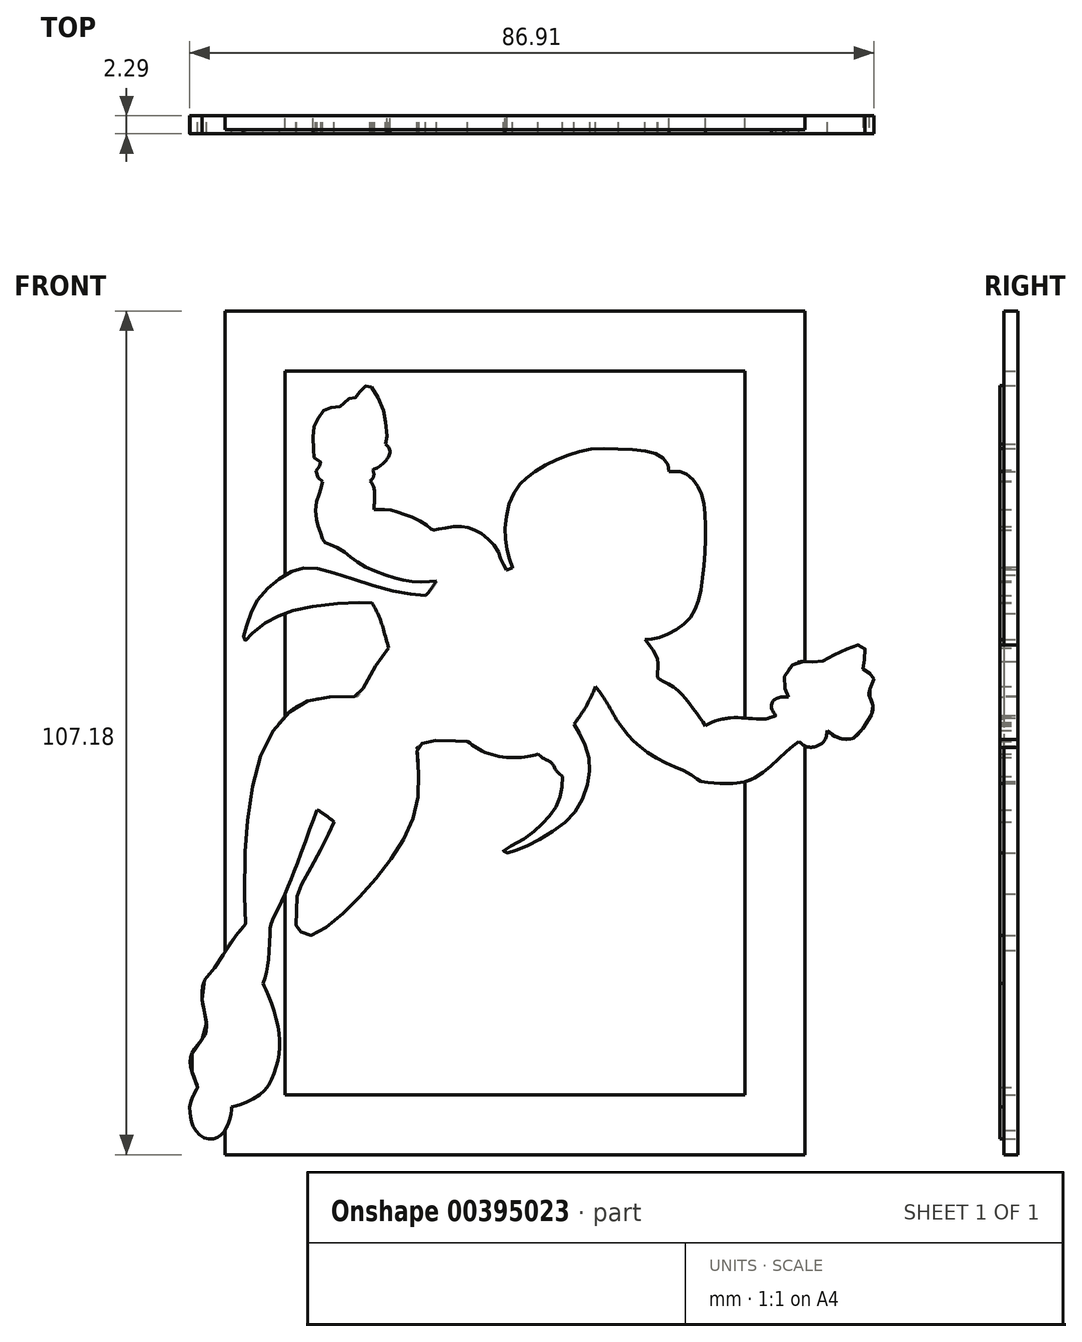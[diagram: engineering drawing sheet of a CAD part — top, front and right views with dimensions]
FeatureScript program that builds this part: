
annotation { "Feature Type Name" : "Feature", "Feature Type Description" : "" }
export const myFeature = defineFeature(function(context is Context, id is Id, definition is map)
    precondition{}
    {
        {
            var Q0;
            Q0=qCreatedBy(makeId("Front.planeOp"),FACE);
            var sketch = newSketch(context, id + "F0", { "sketchPlane" : qUnion([Q0])});
            skLineSegment(sketch, "E0.bottom", {"start": v(36.83, 53.6) * mm, "end": v(-36.83, 53.6) * mm});
            skLineSegment(sketch, "E0.top", {"start": v(36.83, -53.6) * mm, "end": v(-36.83, -53.6) * mm});
            skLineSegment(sketch, "E0.left", {"start": v(36.83, 53.6) * mm, "end": v(36.83, -53.6) * mm});
            skLineSegment(sketch, "E0.right", {"start": v(-36.83, 53.6) * mm, "end": v(-36.83, -53.6) * mm});
            skPoint(sketch, "E0.middle", {"position": v(0, 0) * mm});
            skLineSegment(sketch, "E1.0", {"start": v(-29.2, 45.97) * mm, "end": v(-29.21, -45.97) * mm});
            skLineSegment(sketch, "E1.1", {"start": v(29.21, 45.97) * mm, "end": v(-29.21, 45.97) * mm});
            skLineSegment(sketch, "E1.2", {"start": v(29.21, 45.97) * mm, "end": v(29.21, -45.97) * mm});
            skLineSegment(sketch, "E1.3", {"start": v(29.21, -45.97) * mm, "end": v(-29.21, -45.97) * mm});
            skSolve(sketch);
        }
        {
            var Q0;
            Q0 = qSketchRegion(id + "F0", true);
            extrude(context, id + "F1", {"entities" : qUnion([Q0]), "depth" : 1.78 * mm});
        }
        {
            var Q0;
            Q0=qCreatedBy(makeId("Front.planeOp"),FACE);
            var sketch = newSketch(context, id + "F2", { "sketchPlane" : qUnion([Q0])});
            skFitSpline(sketch, "E2", {"points": [v(-40.3, -45.01) * mm, v(-40.78, -45.94) * mm, v(-41.27, -47.24) * mm, v(-41.23, -48.72) * mm, v(-40.76, -50.17) * mm, v(-39.5, -51.43) * mm, v(-38.13, -51.53) * mm, v(-37.16, -50.92) * mm, v(-36.37, -49.6) * mm, v(-36.03, -48.23) * mm, v(-36, -47.52) * mm], "startDerivative": vector(-5.33, -9.98) * mm, "endDerivative": vector(0.13, 8.86) * mm});
            skFitSpline(sketch, "E3", {"points": [v(-36, -47.52) * mm, v(-34.5, -47.1) * mm, v(-32, -45.62) * mm, v(-30.71, -43.56) * mm, v(-29.96, -40.93) * mm, v(-29.96, -38.24) * mm, v(-30.8, -34.72) * mm, v(-31.82, -32.2) * mm, v(-32.03, -31.86) * mm], "startDerivative": vector(13.23, 2.92) * mm, "endDerivative": vector(-3.23, 4.91) * mm});
            skFitSpline(sketch, "E4", {"points": [v(-32.03, -31.86) * mm, v(-31.5, -30.26) * mm, v(-31.28, -28.32) * mm, v(-31.1, -25.2) * mm, v(-30.92, -24.15) * mm, v(-29.63, -21.38) * mm, v(-28.47, -18.67) * mm, v(-27.04, -14.93) * mm, v(-25.25, -10.08) * mm, v(-25.1, -9.78) * mm], "startDerivative": vector(6.34, 17.06) * mm, "endDerivative": vector(2.36, 4.7) * mm});
            skFitSpline(sketch, "E5", {"points": [v(-25.1, -9.78) * mm, v(-24.1, -10.44) * mm, v(-22.95, -11.3) * mm], "startDerivative": vector(2.08, -1.33) * mm, "endDerivative": vector(2.24, -1.73) * mm});
            skFitSpline(sketch, "E6", {"points": [v(-22.95, -11.3) * mm, v(-23.51, -12.48) * mm, v(-24.6, -14.63) * mm, v(-26.08, -17.48) * mm, v(-27.37, -19.78) * mm, v(-27.68, -20.85) * mm, v(-27.73, -22.57) * mm, v(-27.76, -24.4) * mm, v(-27.76, -24.65) * mm, v(-27.32, -25.16) * mm, v(-26.57, -25.63) * mm, v(-25.47, -25.65) * mm, v(-22.95, -23.9) * mm, v(-19.92, -21.07) * mm, v(-16.69, -17.3) * mm, v(-14.19, -13.64) * mm, v(-12.6, -9.78) * mm, v(-12.22, -5.78) * mm, v(-12.42, -2.04) * mm, v(-12.35, -1.78) * mm, v(-11.33, -1.14) * mm, v(-9.56, -0.98) * mm, v(-6.62, -1.07) * mm, v(-6, -1.1) * mm], "startDerivative": vector(-14.69, -31.4) * mm, "endDerivative": vector(19.63, -1.39) * mm});
            skFitSpline(sketch, "E7", {"points": [v(-6, -1.1) * mm, v(-4.46, -2.16) * mm, v(-1.77, -3.04) * mm, v(1.26, -3.08) * mm, v(2.92, -2.72) * mm], "startDerivative": vector(6.31, -4.9) * mm, "endDerivative": vector(7.12, 1.91) * mm});
            skFitSpline(sketch, "E8", {"points": [v(2.92, -2.72) * mm, v(3.83, -3.35) * mm, v(4.71, -3.86) * mm, v(5.19, -4.7) * mm, v(6.07, -5.54) * mm], "startDerivative": vector(3.4, -2.71) * mm, "endDerivative": vector(3.82, -2.9) * mm});
            skFitSpline(sketch, "E9", {"points": [v(6.07, -5.54) * mm, v(5.9, -7.28) * mm, v(5.4, -9.01) * mm, v(4.28, -10.68) * mm, v(2.92, -12.07) * mm, v(1.1, -13.49) * mm, v(-1.35, -14.88) * mm, v(-1.46, -15.07) * mm, v(-1.12, -15.24) * mm, v(-0.19, -15.03) * mm, v(2.1, -14.12) * mm, v(5.32, -12.14) * mm, v(7.87, -9.78) * mm, v(9.27, -6.32) * mm, v(9.44, -3.47) * mm, v(8.52, -0.66) * mm, v(7.48, 1.1) * mm], "startDerivative": vector(-2.1, -30.1) * mm, "endDerivative": vector(-16.87, 26.04) * mm});
            skFitSpline(sketch, "E10", {"points": [v(7.48, 1.1) * mm, v(8.42, 2.38) * mm, v(9.75, 4.68) * mm, v(10.2, 5.87) * mm], "startDerivative": vector(2.8, 3.6) * mm, "endDerivative": vector(1.25, 3.81) * mm});
            skFitSpline(sketch, "E11", {"points": [v(10.2, 5.87) * mm, v(11.28, 4.46) * mm, v(12.76, 1.93) * mm, v(13.13, 1.33) * mm], "startDerivative": vector(2.94, -3.48) * mm, "endDerivative": vector(1.43, -2.13) * mm});
            skFitSpline(sketch, "E12", {"points": [v(13.13, 1.33) * mm, v(13.98, 0.22) * mm, v(14.91, -0.89) * mm, v(16.07, -1.92) * mm, v(18, -3.2) * mm, v(20.09, -4.23) * mm, v(21.82, -4.98) * mm, v(23.02, -5.77) * mm, v(23.43, -6.06) * mm, v(23.98, -6.25) * mm, v(26.75, -6.44) * mm, v(29.78, -6.04) * mm, v(31.75, -4.86) * mm, v(33.51, -3.3) * mm, v(35.12, -1.83) * mm, v(36.06, -1.1) * mm], "startDerivative": vector(13.91, -18.54) * mm, "endDerivative": vector(16.03, 11.7) * mm});
            skFitSpline(sketch, "E13", {"points": [v(36.06, -1.1) * mm, v(36.47, -1.42) * mm, v(37.02, -1.76) * mm, v(38.35, -1.7) * mm, v(39.32, -0.99) * mm, v(39.58, -0.32) * mm, v(39.7, 0.3) * mm], "startDerivative": vector(3.06, -2.29) * mm, "endDerivative": vector(0.77, 4.22) * mm});
            skFitSpline(sketch, "E14", {"points": [v(39.7, 0.3) * mm, v(40.44, -0.31) * mm, v(40.99, -0.58) * mm, v(41.55, -0.78) * mm, v(42.73, -0.78) * mm, v(44, 0.3) * mm, v(45.31, 2.4) * mm, v(45.5, 3.27) * mm, v(45.27, 4.22) * mm, v(45.01, 4.62) * mm, v(45, 5.33) * mm, v(45.48, 6.53) * mm, v(45.58, 7.01) * mm, v(45.31, 7.4) * mm, v(44.55, 7.82) * mm, v(44.18, 8.2) * mm, v(44.38, 9.11) * mm, v(44.49, 10.33) * mm, v(44.32, 10.96) * mm, v(43.5, 11.16) * mm, v(42.12, 10.65) * mm, v(40.32, 9.78) * mm, v(39.04, 9.1) * mm, v(37.85, 8.97) * mm, v(37.06, 9.01) * mm, v(36.06, 9) * mm, v(34.67, 8.04) * mm, v(34.15, 6.38) * mm, v(34.43, 5.17) * mm, v(34.74, 4.56) * mm], "startDerivative": vector(22.5, -20.66) * mm, "endDerivative": vector(10.79, -19.67) * mm});
            skFitSpline(sketch, "E15", {"points": [v(34.74, 4.56) * mm, v(33.99, 4.56) * mm, v(33.1, 4.28) * mm, v(32.67, 3.8) * mm, v(32.66, 2.97) * mm, v(33.06, 2.3) * mm, v(33.18, 2.2) * mm], "startDerivative": vector(-4, 0.28) * mm, "endDerivative": vector(1.25, -0.88) * mm});
            skFitSpline(sketch, "E16", {"points": [v(33.18, 2.2) * mm, v(32.44, 1.94) * mm, v(31.69, 1.76) * mm, v(29.52, 1.85) * mm, v(27.36, 1.89) * mm, v(25, 1.33) * mm, v(24.22, 0.9) * mm], "startDerivative": vector(-6.23, -2.23) * mm, "endDerivative": vector(-4.82, -3.32) * mm});
            skFitSpline(sketch, "E17", {"points": [v(24.22, 0.9) * mm, v(23.3, 2.2) * mm, v(21.83, 4.13) * mm, v(20.38, 5.67) * mm, v(18.7, 6.64) * mm, v(18.21, 6.95) * mm, v(18.1, 7.17) * mm, v(18.15, 8.18) * mm, v(18.07, 9.5) * mm, v(17.18, 11) * mm, v(16.53, 11.86) * mm], "startDerivative": vector(-7.83, 11.11) * mm, "endDerivative": vector(-6.54, 8.74) * mm});
            skFitSpline(sketch, "E18", {"points": [v(16.53, 11.86) * mm, v(18, 12.02) * mm, v(20.3, 12.97) * mm, v(22.24, 14.61) * mm, v(23.33, 16.92) * mm, v(23.96, 20.98) * mm, v(24.22, 26.04) * mm, v(23.88, 29.74) * mm, v(22.97, 31.7) * mm, v(21.47, 33.04) * mm, v(20.24, 33.18) * mm, v(19.57, 33.18) * mm], "startDerivative": vector(19.3, 0.77) * mm, "endDerivative": vector(-12.81, 0.2) * mm});
            skFitSpline(sketch, "E19", {"points": [v(19.57, 33.18) * mm, v(19.39, 34.17) * mm, v(18.54, 35.08) * mm, v(16.98, 35.73) * mm, v(13.46, 36.04) * mm, v(9.92, 36.06) * mm, v(7.27, 35.45) * mm, v(4.64, 34.4) * mm, v(2.1, 32.86) * mm, v(0.78, 31.75) * mm, v(-0.42, 29.93) * mm, v(-1.17, 26.95) * mm, v(-1.2, 24.6) * mm, v(-0.82, 22.56) * mm, v(-0.28, 20.98) * mm], "startDerivative": vector(-1.11, 21.37) * mm, "endDerivative": vector(9.43, -24.71) * mm});
            skFitSpline(sketch, "E20", {"points": [v(-0.28, 20.98) * mm, v(-0.66, 20.82) * mm, v(-1.06, 20.68) * mm], "startDerivative": vector(-0.77, -0.34) * mm, "endDerivative": vector(-0.81, -0.27) * mm});
            skFitSpline(sketch, "E21", {"points": [v(-1.06, 20.68) * mm, v(-1.7, 21.83) * mm, v(-2.28, 23.31) * mm, v(-3.88, 25.01) * mm, v(-5.58, 25.96) * mm, v(-7, 26.22) * mm, v(-9.04, 26) * mm, v(-10.23, 25.78) * mm, v(-10.43, 25.74) * mm, v(-10.9, 26.12) * mm, v(-12.53, 27.17) * mm, v(-14.58, 27.9) * mm, v(-15.93, 28.35) * mm, v(-17.33, 28.37) * mm, v(-17.92, 28.37) * mm], "startDerivative": vector(-9.8, 15.76) * mm, "endDerivative": vector(-10.94, 0.26) * mm});
            skFitSpline(sketch, "E22", {"points": [v(-17.92, 28.37) * mm, v(-17.83, 29.6) * mm, v(-17.92, 31.16) * mm, v(-18.37, 31.99) * mm], "startDerivative": vector(0.3, 3.5) * mm, "endDerivative": vector(-1.85, 2.5) * mm});
            skFitSpline(sketch, "E23", {"points": [v(-18.37, 31.99) * mm, v(-18.06, 32.35) * mm, v(-17.92, 32.88) * mm, v(-18.06, 33.4) * mm], "startDerivative": vector(1.07, 1.03) * mm, "endDerivative": vector(-0.6, 1.52) * mm});
            skFitSpline(sketch, "E24", {"points": [v(-18.06, 33.4) * mm, v(-17.17, 33.85) * mm, v(-16.4, 34.6) * mm, v(-15.96, 35.26) * mm, v(-15.98, 36.15) * mm, v(-16.44, 36.66) * mm], "startDerivative": vector(4.32, 1.74) * mm, "endDerivative": vector(-3.13, 2.4) * mm});
            skFitSpline(sketch, "E25", {"points": [v(-16.44, 36.66) * mm, v(-16.26, 37.39) * mm, v(-16.44, 39.65) * mm, v(-16.89, 41.47) * mm, v(-18.06, 43.7) * mm, v(-18.59, 44.1) * mm, v(-19.05, 44) * mm, v(-19.7, 43.3) * mm, v(-20.06, 42.75) * mm, v(-20.5, 42.49) * mm, v(-21.15, 42.42) * mm, v(-21.56, 42.08) * mm, v(-21.82, 41.68) * mm, v(-22.15, 41.45) * mm, v(-23.04, 41.33) * mm, v(-23.99, 41.21) * mm, v(-24.7, 40.46) * mm, v(-25.3, 39.4) * mm, v(-25.6, 38.44) * mm, v(-25.63, 36.52) * mm, v(-25.54, 35.14) * mm, v(-25.44, 34.92) * mm, v(-24.67, 34.37) * mm, v(-24.61, 34.23) * mm, v(-24.7, 33.99) * mm, v(-25.14, 33.7) * mm, v(-25.28, 33.08) * mm, v(-25.1, 32.57) * mm, v(-24.65, 32.1) * mm, v(-24.45, 31.95) * mm], "startDerivative": vector(7.06, 17.85) * mm, "endDerivative": vector(9.22, -6.22) * mm});
            skFitSpline(sketch, "E26", {"points": [v(-24.45, 31.95) * mm, v(-24.72, 30.77) * mm, v(-25.22, 29.36) * mm, v(-25.22, 27.2) * mm, v(-24.88, 25.94) * mm, v(-24.45, 24.72) * mm, v(-24.2, 24.26) * mm, v(-23.56, 23.94) * mm, v(-21.98, 23.19) * mm, v(-20.6, 22.11) * mm, v(-18.6, 20.9) * mm, v(-15.67, 19.83) * mm, v(-13.71, 19.3) * mm, v(-11.44, 19.18) * mm, v(-9.95, 19.3) * mm], "startDerivative": vector(-3.11, -19.08) * mm, "endDerivative": vector(20.2, 2.25) * mm});
            skFitSpline(sketch, "E27", {"points": [v(-9.95, 19.3) * mm, v(-10.76, 18.1) * mm, v(-11.34, 17.44) * mm], "startDerivative": vector(-1.48, -2.3) * mm, "endDerivative": vector(-1.3, -1.38) * mm});
            skFitSpline(sketch, "E28", {"points": [v(-11.34, 17.44) * mm, v(-13.9, 17.7) * mm, v(-17.99, 18.7) * mm, v(-22.43, 20.13) * mm, v(-25.44, 20.9) * mm, v(-27.35, 20.86) * mm, v(-29.1, 20.1) * mm, v(-31.03, 18.68) * mm, v(-32.67, 16.9) * mm, v(-33.54, 15.18) * mm, v(-34.26, 12.97) * mm, v(-34.53, 12.06) * mm, v(-34.49, 11.8) * mm, v(-34.22, 11.76) * mm, v(-33.74, 12.28) * mm, v(-31.57, 14.04) * mm, v(-29.49, 15.07) * mm, v(-26.2, 15.99) * mm, v(-20.08, 16.53) * mm, v(-18.15, 16.5) * mm], "startDerivative": vector(-42.33, 2.89) * mm, "endDerivative": vector(32.1, -1.6) * mm});
            skFitSpline(sketch, "E29", {"points": [v(-18.15, 16.5) * mm, v(-17.34, 14.95) * mm, v(-16.75, 13.29) * mm, v(-16.05, 10.76) * mm], "startDerivative": vector(2.82, -5) * mm, "endDerivative": vector(1.9, -7.03) * mm});
            skFitSpline(sketch, "E30", {"points": [v(-16.05, 10.76) * mm, v(-17.53, 8.78) * mm, v(-19.2, 5.9) * mm, v(-19.96, 4.6) * mm, v(-20.1, 4.58) * mm, v(-22.48, 4.6) * mm, v(-25.46, 4.29) * mm, v(-27.37, 3.52) * mm, v(-29.5, 1.89) * mm, v(-31.52, -1.17) * mm, v(-33.01, -5.27) * mm, v(-33.95, -11.1) * mm, v(-34.33, -16.85) * mm, v(-34.24, -24.15) * mm, v(-34.27, -24.38) * mm, v(-35.04, -25.35) * mm, v(-36.47, -26.98) * mm, v(-37.7, -29.53) * mm, v(-37.99, -29.73) * mm, v(-38.96, -30.73) * mm, v(-39.48, -31.56) * mm, v(-39.73, -33.64) * mm, v(-39.25, -36.5) * mm, v(-39.3, -38.25) * mm, v(-40.08, -39.34) * mm, v(-41.02, -40.74) * mm, v(-41.22, -42.43) * mm, v(-40.53, -44.32) * mm, v(-40.3, -45.01) * mm], "startDerivative": vector(-38.64, -47.42) * mm, "endDerivative": vector(8.26, -28.9) * mm});
            skSolve(sketch);
        }
        {
            var Q0;
            Q0 = qSketchRegion(id + "F2", true);
            extrude(context, id + "F3", {"entities" : qUnion([Q0]), "operationType" : NewBodyOperationType.ADD, "depth" : 2.3 * mm});
        }
        {
            var Q0;
            Q0=makeQuery(id+"F3.opExtrude","CAP_FACE",FACE,{"disambiguationData":[OSD([sQuery(id+"F2.wireOp",EDGE,"E2"),sQuery(id+"F2.wireOp",EDGE,"E3"),sQuery(id+"F2.wireOp",EDGE,"E4"),sQuery(id+"F2.wireOp",EDGE,"E5"),sQuery(id+"F2.wireOp",EDGE,"E6"),sQuery(id+"F2.wireOp",EDGE,"E7"),sQuery(id+"F2.wireOp",EDGE,"E8"),sQuery(id+"F2.wireOp",EDGE,"E9"),sQuery(id+"F2.wireOp",EDGE,"E10"),sQuery(id+"F2.wireOp",EDGE,"E11"),sQuery(id+"F2.wireOp",EDGE,"E12"),sQuery(id+"F2.wireOp",EDGE,"E13"),sQuery(id+"F2.wireOp",EDGE,"E14"),sQuery(id+"F2.wireOp",EDGE,"E15"),sQuery(id+"F2.wireOp",EDGE,"E16"),sQuery(id+"F2.wireOp",EDGE,"E17"),sQuery(id+"F2.wireOp",EDGE,"E18"),sQuery(id+"F2.wireOp",EDGE,"E19"),sQuery(id+"F2.wireOp",EDGE,"E20"),sQuery(id+"F2.wireOp",EDGE,"E21"),sQuery(id+"F2.wireOp",EDGE,"E22"),sQuery(id+"F2.wireOp",EDGE,"E23"),sQuery(id+"F2.wireOp",EDGE,"E24"),sQuery(id+"F2.wireOp",EDGE,"E25"),sQuery(id+"F2.wireOp",EDGE,"E26"),sQuery(id+"F2.wireOp",EDGE,"E27"),sQuery(id+"F2.wireOp",EDGE,"E28"),sQuery(id+"F2.wireOp",EDGE,"E29"),sQuery(id+"F2.wireOp",EDGE,"E30")])],"isStart":false});
            var sketch = newSketch(context, id + "F4", { "sketchPlane" : qUnion([Q0])});
            skFitSpline(sketch, "E31", {"points": [v(6.33, 20.8) * mm, v(6.52, 21.07) * mm, v(6.8, 21.26) * mm, v(7.13, 21.28) * mm], "startDerivative": vector(0.5, 0.86) * mm, "endDerivative": vector(1.04, -0.07) * mm});
            skFitSpline(sketch, "E32", {"points": [v(14.02, 16.77) * mm, v(13.22, 16.62) * mm, v(12.18, 16.57) * mm, v(10.86, 16.87) * mm, v(9.92, 17.2) * mm], "startDerivative": vector(-3.53, -0.74) * mm, "endDerivative": vector(-3.62, 1.3) * mm});
            skFitSpline(sketch, "E33", {"points": [v(7.1, 20.4) * mm, v(7.64, 19.66) * mm, v(8.02, 19.03) * mm, v(8.36, 18.6) * mm], "startDerivative": vector(1.56, -1.95) * mm, "endDerivative": vector(1.2, -1.43) * mm});
            skFitSpline(sketch, "E34", {"points": [v(6.9, 19.34) * mm, v(6.9, 18.4) * mm, v(7.15, 17.57) * mm, v(7.93, 16.58) * mm, v(8.88, 15.8) * mm, v(10.1, 15.46) * mm, v(11.16, 15.78) * mm, v(11.72, 16.41) * mm], "startDerivative": vector(-0.34, -7.15) * mm, "endDerivative": vector(3.77, 5.4) * mm});
            skFitSpline(sketch, "E35", {"points": [v(7.91, 20.38) * mm, v(9.12, 19.93) * mm, v(10.45, 19.19) * mm, v(11.45, 18.49) * mm, v(12.05, 17.8) * mm, v(12.63, 17.06) * mm, v(13.1, 16.79) * mm], "startDerivative": vector(6.48, -2.05) * mm, "endDerivative": vector(4, -1.7) * mm});
            skFitSpline(sketch, "E36", {"points": [v(13.88, 17.14) * mm, v(14.14, 16.89) * mm, v(14.26, 16.6) * mm], "startDerivative": vector(0.56, -0.46) * mm, "endDerivative": vector(0.19, -0.63) * mm});
            skCircle(sketch, "E37", {"center": v(11.13, 20.67) * mm, "radius": 0.18 * mm});
            skCircle(sketch, "E38", {"center": v(11.88, 19.95) * mm, "radius": 0.28 * mm});
            skFitSpline(sketch, "E39", {"points": [v(10.55, 26.04) * mm, v(10.32, 25.81) * mm, v(10.08, 25.47) * mm, v(10.16, 25) * mm, v(10.4, 24.68) * mm, v(11.07, 24.88) * mm, v(11.21, 25.05) * mm], "startDerivative": vector(-1.43, -1.43) * mm, "endDerivative": vector(0.7, 1.26) * mm});
            skFitSpline(sketch, "E40", {"points": [v(8.8, 25.47) * mm, v(8.93, 26.06) * mm, v(9.45, 26.44) * mm, v(10.32, 26.48) * mm, v(11, 25.83) * mm, v(11.4, 25.2) * mm, v(11.58, 24.26) * mm], "startDerivative": vector(0.26, 4.34) * mm, "endDerivative": vector(0.61, -5.55) * mm});
            skFitSpline(sketch, "E41", {"points": [v(15.32, 22.5) * mm, v(15.12, 22.03) * mm, v(15.08, 21.5) * mm, v(15.4, 21.28) * mm, v(15.95, 21.28) * mm, v(16.45, 21.85) * mm, v(16.57, 22.05) * mm], "startDerivative": vector(-1.27, -2.54) * mm, "endDerivative": vector(0.81, 1.4) * mm});
            skFitSpline(sketch, "E42", {"points": [v(14.17, 22.11) * mm, v(14.96, 22.52) * mm, v(15.54, 22.68) * mm, v(16.41, 22.5) * mm, v(17.12, 21.87) * mm, v(17.3, 21.28) * mm, v(17.1, 20.84) * mm, v(16.57, 20.53) * mm], "startDerivative": vector(5.17, 2.8) * mm, "endDerivative": vector(-4.44, -1.94) * mm});
            skFitSpline(sketch, "E43", {"points": [v(9.88, 28.02) * mm, v(10.79, 28.38) * mm, v(12.08, 28.65) * mm, v(12.59, 28.63) * mm, v(12.83, 28.44) * mm, v(12.77, 27.88) * mm, v(12.71, 26.7) * mm, v(12.81, 26.06) * mm, v(13.2, 25.81) * mm, v(13.62, 25.77) * mm], "startDerivative": vector(6.17, 2.86) * mm, "endDerivative": vector(4.76, -0.05) * mm});
            skFitSpline(sketch, "E44", {"points": [v(15.62, 24.34) * mm, v(15.93, 24.07) * mm, v(16.55, 24.18) * mm, v(17.44, 24.64) * mm, v(18.1, 25.05) * mm, v(18.3, 25.07) * mm, v(18.46, 24.92) * mm, v(18.5, 24.66) * mm], "startDerivative": vector(1.95, -2.5) * mm, "endDerivative": vector(0.03, -2.59) * mm});
            skFitSpline(sketch, "E45", {"points": [v(17.32, 28.18) * mm, v(18.31, 28.63) * mm, v(19.47, 28.93) * mm, v(20.28, 28.93) * mm], "startDerivative": vector(2.77, 1.35) * mm, "endDerivative": vector(2.6, -0.18) * mm});
            skFitSpline(sketch, "E46", {"points": [v(10.75, 33.85) * mm, v(10.24, 33.28) * mm, v(10.02, 32.71) * mm, v(10.04, 32.6) * mm, v(10.85, 32.87) * mm, v(12.23, 33.14) * mm, v(12.55, 33.22) * mm, v(12.71, 33.3) * mm, v(13.03, 33.8) * mm, v(13.28, 34.19) * mm, v(13.26, 34.31) * mm, v(12.75, 34.2) * mm, v(12.02, 34.17) * mm, v(11.17, 34.09) * mm, v(10.75, 33.85) * mm]});
            skFitSpline(sketch, "E47", {"points": [v(-0.1, 20.83) * mm, v(0.34, 20.08) * mm, v(1.4, 19.03) * mm, v(2.69, 18.14) * mm, v(4.57, 17.92) * mm, v(5.74, 18.08) * mm, v(5.83, 18.16) * mm, v(5.66, 18.26) * mm, v(4.87, 18.93) * mm, v(4.02, 20.49) * mm, v(4.07, 22.2) * mm, v(5.48, 25.12) * mm, v(7.12, 26.98) * mm, v(9.59, 29.03) * mm, v(13.2, 30.48) * mm, v(15.03, 30.8) * mm, v(15.93, 30.6) * mm, v(15.93, 29.96) * mm, v(15.7, 29.09) * mm, v(15.68, 28.68) * mm], "startDerivative": vector(8.68, -17.41) * mm, "endDerivative": vector(0.36, -12.73) * mm});
            skFitSpline(sketch, "E48", {"points": [v(17.74, 27.25) * mm, v(18.67, 27.49) * mm, v(19.97, 27.37) * mm, v(20.15, 26.86) * mm, v(19.82, 24.45) * mm, v(19.01, 22.15) * mm, v(18.1, 19.68) * mm, v(17.17, 17.88) * mm, v(15.93, 16.32) * mm, v(14.73, 15.35) * mm, v(13.2, 14.44) * mm, v(12.64, 14.26) * mm, v(12.14, 14.18) * mm, v(9.83, 14.08) * mm, v(9.04, 13.87) * mm, v(8.15, 14.04) * mm, v(7, 14.72) * mm, v(5.93, 15.65) * mm, v(5.7, 16.32) * mm, v(5.36, 17.03) * mm, v(5.16, 17.62) * mm], "startDerivative": vector(19, 6.88) * mm, "endDerivative": vector(-4.68, 16.61) * mm});
            skFitSpline(sketch, "E49", {"points": [v(16.37, 11.86) * mm, v(15.2, 12.01) * mm, v(13.89, 12.36) * mm, v(12.64, 12.97) * mm, v(11.88, 13.56) * mm], "startDerivative": vector(-4.7, 0.48) * mm, "endDerivative": vector(-3.15, 2.68) * mm});
            skSolve(sketch);
        }
        {
            var Q0;
            Q0 = qSketchRegion(id + "F4", true);
            var Q1;
            Q1=sQuery(id+"F4.wireOp",EDGE,"E47");
            var Q2;
            Q2=sQuery(id+"F4.wireOp",EDGE,"E48");
            var Q3;
            Q3=sQuery(id+"F4.wireOp",EDGE,"E34");
            var Q4;
            Q4=sQuery(id+"F4.wireOp",EDGE,"E32");
            var Q5;
            Q5=sQuery(id+"F4.wireOp",EDGE,"E46");
            var Q6;
            Q6=sQuery(id+"F4.wireOp",EDGE,"E38");
            var Q7;
            Q7=sQuery(id+"F4.wireOp",EDGE,"E37");
            var Q8;
            Q8=sQuery(id+"F4.wireOp",EDGE,"E35");
            var Q9;
            Q9=sQuery(id+"F4.wireOp",EDGE,"E33");
            var Q10;
            Q10=sQuery(id+"F4.wireOp",EDGE,"E31");
            var Q11;
            Q11=sQuery(id+"F4.wireOp",EDGE,"E36");
            var Q12;
            Q12=sQuery(id+"F4.wireOp",EDGE,"E41");
            var Q13;
            Q13=sQuery(id+"F4.wireOp",EDGE,"E42");
            var Q14;
            Q14=sQuery(id+"F4.wireOp",EDGE,"E44");
            var Q15;
            Q15=sQuery(id+"F4.wireOp",EDGE,"E45");
            var Q16;
            Q16=sQuery(id+"F4.wireOp",EDGE,"E43");
            var Q17;
            Q17=sQuery(id+"F4.wireOp",EDGE,"E39");
            var Q18;
            Q18=sQuery(id+"F4.wireOp",EDGE,"E40");
            var Q19;
            Q19=sQuery(id+"F4.wireOp",EDGE,"E49");
            extrude(context, id + "F5", {"entities" : qUnion([Q0]), "bodyType" : ToolBodyType.SURFACE, "surfaceEntities" : qUnion([Q1, Q2, Q3, Q4, Q5, Q6, Q7, Q8, Q9, Q10, Q11, Q12, Q13, Q14, Q15, Q16, Q17, Q18, Q19]), "depth" : 0.25 * mm});
        }
        {
            var Q0;
            Q0=makeQuery(id+"F3.opExtrude","CAP_FACE",FACE,{"disambiguationData":[OSD([sQuery(id+"F2.wireOp",EDGE,"E2"),sQuery(id+"F2.wireOp",EDGE,"E3"),sQuery(id+"F2.wireOp",EDGE,"E4"),sQuery(id+"F2.wireOp",EDGE,"E5"),sQuery(id+"F2.wireOp",EDGE,"E6"),sQuery(id+"F2.wireOp",EDGE,"E7"),sQuery(id+"F2.wireOp",EDGE,"E8"),sQuery(id+"F2.wireOp",EDGE,"E9"),sQuery(id+"F2.wireOp",EDGE,"E10"),sQuery(id+"F2.wireOp",EDGE,"E11"),sQuery(id+"F2.wireOp",EDGE,"E12"),sQuery(id+"F2.wireOp",EDGE,"E13"),sQuery(id+"F2.wireOp",EDGE,"E14"),sQuery(id+"F2.wireOp",EDGE,"E15"),sQuery(id+"F2.wireOp",EDGE,"E16"),sQuery(id+"F2.wireOp",EDGE,"E17"),sQuery(id+"F2.wireOp",EDGE,"E18"),sQuery(id+"F2.wireOp",EDGE,"E19"),sQuery(id+"F2.wireOp",EDGE,"E20"),sQuery(id+"F2.wireOp",EDGE,"E21"),sQuery(id+"F2.wireOp",EDGE,"E22"),sQuery(id+"F2.wireOp",EDGE,"E23"),sQuery(id+"F2.wireOp",EDGE,"E24"),sQuery(id+"F2.wireOp",EDGE,"E25"),sQuery(id+"F2.wireOp",EDGE,"E26"),sQuery(id+"F2.wireOp",EDGE,"E27"),sQuery(id+"F2.wireOp",EDGE,"E28"),sQuery(id+"F2.wireOp",EDGE,"E29"),sQuery(id+"F2.wireOp",EDGE,"E30")])],"isStart":false});
            var sketch = newSketch(context, id + "F6", { "sketchPlane" : qUnion([Q0])});
            skFitSpline(sketch, "E50", {"points": [v(-24.37, 34.22) * mm, v(-23.08, 34.14) * mm, v(-20.8, 34.47) * mm, v(-17.8, 35.64) * mm, v(-16.53, 36.56) * mm], "startDerivative": vector(6.14, -0.64) * mm, "endDerivative": vector(4.9, 4.13) * mm});
            skFitSpline(sketch, "E51", {"points": [v(-23.3, 34.4) * mm, v(-23.64, 35.3) * mm, v(-23.8, 37.05) * mm, v(-23.8, 38.08) * mm], "startDerivative": vector(-1.3, 2.68) * mm, "endDerivative": vector(0.04, 3.06) * mm});
            skFitSpline(sketch, "E52", {"points": [v(-21.7, 34.51) * mm, v(-22, 35.64) * mm, v(-22.08, 37.91) * mm, v(-21.98, 38.85) * mm], "startDerivative": vector(-1.08, 3.22) * mm, "endDerivative": vector(0.45, 2.92) * mm});
            skFitSpline(sketch, "E53", {"points": [v(-19.17, 35.23) * mm, v(-19.82, 36.84) * mm, v(-20.1, 38.99) * mm, v(-20.12, 40.21) * mm], "startDerivative": vector(-2.15, 4.44) * mm, "endDerivative": vector(0.03, 3.94) * mm});
            skFitSpline(sketch, "E54", {"points": [v(-18.23, 33.31) * mm, v(-19.03, 33.1) * mm, v(-19.89, 33.1) * mm, v(-20.73, 33.4) * mm, v(-20.79, 34.04) * mm, v(-20.7, 34.37) * mm], "startDerivative": vector(-3.66, -1.18) * mm, "endDerivative": vector(0.6, 2.06) * mm});
            skFitSpline(sketch, "E55", {"points": [v(-24.34, 31.95) * mm, v(-23.81, 31.95) * mm, v(-23.3, 32.13) * mm, v(-23.08, 32.98) * mm], "startDerivative": vector(1.7, -0.07) * mm, "endDerivative": vector(0.27, 2.6) * mm});
            skFitSpline(sketch, "E56", {"points": [v(-23.08, 32.1) * mm, v(-22.77, 31.7) * mm, v(-22.15, 31.28) * mm, v(-21.2, 31.32) * mm, v(-20.63, 31.73) * mm, v(-20.35, 32.43) * mm], "startDerivative": vector(1.63, -2.39) * mm, "endDerivative": vector(1.1, 3.7) * mm});
            skFitSpline(sketch, "E57", {"points": [v(-20.28, 32.3) * mm, v(-19.9, 31.95) * mm, v(-19.07, 31.83) * mm, v(-18.47, 31.95) * mm], "startDerivative": vector(1.01, -1.36) * mm, "endDerivative": vector(1.7, 0.48) * mm});
            skFitSpline(sketch, "E58", {"points": [v(33.37, 2.15) * mm, v(34.08, 2) * mm, v(34.56, 2.37) * mm, v(35.03, 2.73) * mm], "startDerivative": vector(2.13, -0.82) * mm, "endDerivative": vector(1.47, 1.04) * mm});
            skFitSpline(sketch, "E59", {"points": [v(34.08, 1.8) * mm, v(34, 0.85) * mm, v(34.44, -0.06) * mm, v(35.53, -0.48) * mm, v(36.87, 0.3) * mm, v(37.41, 1.18) * mm], "startDerivative": vector(-1, -5.18) * mm, "endDerivative": vector(2.19, 4.57) * mm});
            skFitSpline(sketch, "E60", {"points": [v(35.99, -0.98) * mm, v(35.97, -0.48) * mm], "startDerivative": vector(-0.02, 0.5) * mm, "endDerivative": vector(-0.02, 0.5) * mm});
            skFitSpline(sketch, "E61", {"points": [v(34.81, 4.5) * mm, v(35.53, 3.73) * mm, v(36.4, 2.82) * mm, v(37.22, 2.18) * mm, v(38.46, 1.96) * mm, v(39.42, 2.53) * mm, v(39.7, 3.99) * mm, v(39.35, 5.27) * mm, v(38.54, 6.47) * mm, v(37.57, 7.54) * mm], "startDerivative": vector(6.88, -7.33) * mm, "endDerivative": vector(-8.33, 8.8) * mm});
            skFitSpline(sketch, "E62", {"points": [v(38.96, 8.14) * mm, v(38.51, 7.56) * mm, v(38.4, 6.84) * mm], "startDerivative": vector(-1.05, -1.08) * mm, "endDerivative": vector(-0.08, -1.5) * mm});
            skFitSpline(sketch, "E63", {"points": [v(39.7, 4.92) * mm, v(40.17, 4.77) * mm, v(41, 5.16) * mm, v(42.73, 6.57) * mm, v(43.22, 7.08) * mm], "startDerivative": vector(2.62, -1.3) * mm, "endDerivative": vector(1.77, 2.1) * mm});
            skFitSpline(sketch, "E64", {"points": [v(38.96, 1.85) * mm, v(39.15, 1.58) * mm, v(39.7, 1.5) * mm, v(40.93, 2.03) * mm, v(42.88, 3.44) * mm, v(43.9, 4.35) * mm], "startDerivative": vector(1.34, -2.68) * mm, "endDerivative": vector(4.02, 3.77) * mm});
            skFitSpline(sketch, "E65", {"points": [v(39.7, 0.43) * mm, v(39.4, 0.85) * mm, v(39.32, 1.38) * mm], "startDerivative": vector(-0.73, 0.8) * mm, "endDerivative": vector(-0.02, 1.1) * mm});
            skFitSpline(sketch, "E66", {"points": [v(40.6, -0.18) * mm, v(41.21, -0.1) * mm, v(42.49, 0.96) * mm, v(43.42, 1.82) * mm, v(44.04, 2.47) * mm], "startDerivative": vector(3, -0.26) * mm, "endDerivative": vector(2.59, 2.82) * mm});
            skFitSpline(sketch, "E67", {"points": [v(-17.92, 28.24) * mm, v(-17.92, 27.85) * mm, v(-17.88, 27.6) * mm], "startDerivative": vector(-0.02, -0.75) * mm, "endDerivative": vector(0.1, -0.55) * mm});
            skFitSpline(sketch, "E68", {"points": [v(-10.31, 25.58) * mm, v(-9.78, 25.1) * mm, v(-9.4, 24.74) * mm], "startDerivative": vector(1.03, -0.93) * mm, "endDerivative": vector(0.8, -0.75) * mm});
            skFitSpline(sketch, "E69", {"points": [v(24.15, 0.83) * mm, v(23.9, 0.6) * mm, v(23.7, 0.34) * mm], "startDerivative": vector(-0.5, -0.43) * mm, "endDerivative": vector(-0.38, -0.54) * mm});
            skSolve(sketch);
        }
        {
            var Q0;
            Q0 = qSketchRegion(id + "F6", true);
            var Q1;
            Q1=sQuery(id+"F6.wireOp",EDGE,"E58");
            var Q2;
            Q2=sQuery(id+"F6.wireOp",EDGE,"E59");
            var Q3;
            Q3=sQuery(id+"F6.wireOp",EDGE,"E60");
            var Q4;
            Q4=sQuery(id+"F6.wireOp",EDGE,"E66");
            var Q5;
            Q5=sQuery(id+"F6.wireOp",EDGE,"E65");
            var Q6;
            Q6=sQuery(id+"F6.wireOp",EDGE,"E64");
            var Q7;
            Q7=sQuery(id+"F6.wireOp",EDGE,"E61");
            var Q8;
            Q8=sQuery(id+"F6.wireOp",EDGE,"E63");
            var Q9;
            Q9=sQuery(id+"F6.wireOp",EDGE,"E62");
            var Q10;
            Q10=sQuery(id+"F6.wireOp",EDGE,"E55");
            var Q11;
            Q11=sQuery(id+"F6.wireOp",EDGE,"E56");
            var Q12;
            Q12=sQuery(id+"F6.wireOp",EDGE,"E57");
            var Q13;
            Q13=sQuery(id+"F6.wireOp",EDGE,"E54");
            var Q14;
            Q14=sQuery(id+"F6.wireOp",EDGE,"E50");
            var Q15;
            Q15=sQuery(id+"F6.wireOp",EDGE,"E53");
            var Q16;
            Q16=sQuery(id+"F6.wireOp",EDGE,"E52");
            var Q17;
            Q17=sQuery(id+"F6.wireOp",EDGE,"E51");
            var Q18;
            Q18=sQuery(id+"F6.wireOp",EDGE,"E69");
            var Q19;
            Q19=sQuery(id+"F6.wireOp",EDGE,"E68");
            var Q20;
            Q20=sQuery(id+"F6.wireOp",EDGE,"E67");
            extrude(context, id + "F7", {"entities" : qUnion([Q0]), "bodyType" : ToolBodyType.SURFACE, "surfaceEntities" : qUnion([Q1, Q2, Q3, Q4, Q5, Q6, Q7, Q8, Q9, Q10, Q11, Q12, Q13, Q14, Q15, Q16, Q17, Q18, Q19, Q20]), "depth" : 0.25 * mm});
        }
        {
            var Q0;
            Q0=makeQuery(id+"F3.opExtrude","CAP_FACE",FACE,{"disambiguationData":[OSD([sQuery(id+"F2.wireOp",EDGE,"E2"),sQuery(id+"F2.wireOp",EDGE,"E3"),sQuery(id+"F2.wireOp",EDGE,"E4"),sQuery(id+"F2.wireOp",EDGE,"E5"),sQuery(id+"F2.wireOp",EDGE,"E6"),sQuery(id+"F2.wireOp",EDGE,"E7"),sQuery(id+"F2.wireOp",EDGE,"E8"),sQuery(id+"F2.wireOp",EDGE,"E9"),sQuery(id+"F2.wireOp",EDGE,"E10"),sQuery(id+"F2.wireOp",EDGE,"E11"),sQuery(id+"F2.wireOp",EDGE,"E12"),sQuery(id+"F2.wireOp",EDGE,"E13"),sQuery(id+"F2.wireOp",EDGE,"E14"),sQuery(id+"F2.wireOp",EDGE,"E15"),sQuery(id+"F2.wireOp",EDGE,"E16"),sQuery(id+"F2.wireOp",EDGE,"E17"),sQuery(id+"F2.wireOp",EDGE,"E18"),sQuery(id+"F2.wireOp",EDGE,"E19"),sQuery(id+"F2.wireOp",EDGE,"E20"),sQuery(id+"F2.wireOp",EDGE,"E21"),sQuery(id+"F2.wireOp",EDGE,"E22"),sQuery(id+"F2.wireOp",EDGE,"E23"),sQuery(id+"F2.wireOp",EDGE,"E24"),sQuery(id+"F2.wireOp",EDGE,"E25"),sQuery(id+"F2.wireOp",EDGE,"E26"),sQuery(id+"F2.wireOp",EDGE,"E27"),sQuery(id+"F2.wireOp",EDGE,"E28"),sQuery(id+"F2.wireOp",EDGE,"E29"),sQuery(id+"F2.wireOp",EDGE,"E30")])],"isStart":false});
            var sketch = newSketch(context, id + "F8", { "sketchPlane" : qUnion([Q0])});
            skFitSpline(sketch, "E70", {"points": [v(-11.47, 17.3) * mm, v(-11.94, 16.66) * mm, v(-12.3, 16.02) * mm, v(-13.67, 13.82) * mm, v(-14.84, 12.02) * mm, v(-15.87, 10.9) * mm], "startDerivative": vector(-3.5, -4.53) * mm, "endDerivative": vector(-5.2, -5.17) * mm});
            skFitSpline(sketch, "E71", {"points": [v(-17.75, 16.5) * mm, v(-15.5, 16.5) * mm, v(-13.4, 16.35) * mm, v(-12.36, 16.22) * mm], "startDerivative": vector(5.86, 0.1) * mm, "endDerivative": vector(3.64, -0.46) * mm});
            skFitSpline(sketch, "E72", {"points": [v(0.52, 17.71) * mm, v(0.44, 17.2) * mm, v(0.47, 16.7) * mm], "startDerivative": vector(-0.2, -1.02) * mm, "endDerivative": vector(0.1, -0.98) * mm});
            skFitSpline(sketch, "E73", {"points": [v(-0.6, 15.54) * mm, v(-0.54, 14.94) * mm, v(-0.46, 14.45) * mm], "startDerivative": vector(0.1, -1.18) * mm, "endDerivative": vector(0.2, -1) * mm});
            skFitSpline(sketch, "E74", {"points": [v(1.29, 15.05) * mm, v(1.32, 14.62) * mm], "startDerivative": vector(0.03, -0.43) * mm, "endDerivative": vector(0.03, -0.43) * mm});
            skFitSpline(sketch, "E75", {"points": [v(-1.2, 20.43) * mm, v(-1.67, 18.58) * mm, v(-2.14, 16.77) * mm, v(-2.26, 14.3) * mm, v(-1.44, 11.92) * mm, v(0.4, 9.34) * mm, v(2.09, 8) * mm, v(4.65, 7.24) * mm, v(8.03, 7.38) * mm, v(10.39, 7.98) * mm, v(10.64, 8.08) * mm, v(11.59, 9.34) * mm, v(12.73, 11.06) * mm, v(13.1, 11.5) * mm, v(13.48, 12.09) * mm], "startDerivative": vector(-6.3, -25.8) * mm, "endDerivative": vector(8.54, 14.58) * mm});
            skFitSpline(sketch, "E76", {"points": [v(9.4, 9.92) * mm, v(10.46, 10.1) * mm, v(11.82, 10.53) * mm, v(12.36, 10.86) * mm], "startDerivative": vector(2.9, 0.42) * mm, "endDerivative": vector(1.74, 1.25) * mm});
            skFitSpline(sketch, "E77", {"points": [v(10.27, 6.24) * mm, v(10.56, 7.13) * mm, v(10.7, 7.93) * mm], "startDerivative": vector(0.62, 1.73) * mm, "endDerivative": vector(0.23, 1.64) * mm});
            skFitSpline(sketch, "E78", {"points": [v(-6.35, -0.83) * mm, v(-8.09, 0.95) * mm, v(-10.27, 3.66) * mm, v(-11.7, 6.03) * mm, v(-12.03, 7.06) * mm, v(-12.18, 7.85) * mm, v(-12.26, 9.08) * mm, v(-12.26, 10.56) * mm, v(-12.12, 11.51) * mm], "startDerivative": vector(-11.12, 10.92) * mm, "endDerivative": vector(1.82, 9.4) * mm});
            skFitSpline(sketch, "E79", {"points": [v(-4.29, 5.68) * mm, v(-4.33, 4.05) * mm, v(-4.61, 2.18) * mm, v(-4.77, 1.1) * mm, v(-4.75, 0.85) * mm, v(-4.39, 0.85) * mm, v(-2.55, 0.95) * mm, v(-0.6, 1.3) * mm, v(-0.1, 1.5) * mm, v(0.06, 1.66) * mm, v(0.37, 3.28) * mm, v(0.57, 5.9) * mm, v(0.5, 6.43) * mm, v(0.4, 6.5) * mm, v(0, 6.35) * mm, v(-1.56, 6.03) * mm, v(-3.38, 5.85) * mm, v(-3.94, 5.83) * mm, v(-4.08, 5.8) * mm, v(-4.23, 5.77) * mm, v(-4.29, 5.68) * mm]});
            skFitSpline(sketch, "E80", {"points": [v(-9.3, -0.72) * mm, v(-11.19, 0.38) * mm, v(-13.15, 2.48) * mm, v(-14.9, 5.07) * mm, v(-16.14, 7.58) * mm, v(-16.57, 9.68) * mm], "startDerivative": vector(-10.48, 5.08) * mm, "endDerivative": vector(-1.55, 11.46) * mm});
            skFitSpline(sketch, "E81", {"points": [v(-9.99, 18.64) * mm, v(-7.8, 18.82) * mm, v(-4.62, 19.17) * mm, v(-2.48, 19.68) * mm, v(-1.63, 19.84) * mm], "startDerivative": vector(7.9, 0.7) * mm, "endDerivative": vector(4.66, 0.72) * mm});
            skFitSpline(sketch, "E82", {"points": [v(3.13, -2.53) * mm, v(4.77, -1.6) * mm, v(6.57, 0.19) * mm, v(7.32, 0.87) * mm], "startDerivative": vector(4.67, 2.13) * mm, "endDerivative": vector(2.64, 2.22) * mm});
            skFitSpline(sketch, "E83", {"points": [v(5.4, -1.32) * mm, v(5.72, -2.1) * mm, v(6.07, -3.59) * mm, v(6.07, -5.22) * mm], "startDerivative": vector(1.2, -2.66) * mm, "endDerivative": vector(-0.25, -4.36) * mm});
            skFitSpline(sketch, "E84", {"points": [v(-19.1, -2.15) * mm, v(-19.41, -2.6) * mm], "startDerivative": vector(-0.3, -0.44) * mm, "endDerivative": vector(-0.3, -0.44) * mm});
            skFitSpline(sketch, "E85", {"points": [v(-27.1, 3.23) * mm, v(-26.62, 1.29) * mm, v(-24.79, -2.25) * mm, v(-21.86, -5.35) * mm, v(-18.05, -7.63) * mm, v(-15.77, -8.17) * mm, v(-12.68, -8.2) * mm], "startDerivative": vector(2.47, -13.8) * mm, "endDerivative": vector(20.24, 0.37) * mm});
            skFitSpline(sketch, "E86", {"points": [v(-37.7, -29.76) * mm, v(-37.68, -31.41) * mm, v(-36.98, -33.67) * mm, v(-36.11, -34.73) * mm, v(-34.8, -35.34) * mm, v(-33.8, -35.1) * mm, v(-32.58, -32.94) * mm, v(-32.17, -32.1) * mm], "startDerivative": vector(-0.71, -10.5) * mm, "endDerivative": vector(3.15, 6.07) * mm});
            skFitSpline(sketch, "E87", {"points": [v(-40.15, -45.15) * mm, v(-39.14, -46.12) * mm, v(-37.97, -47.08) * mm, v(-36.98, -47.48) * mm, v(-36.11, -47.52) * mm], "startDerivative": vector(3.6, -3.56) * mm, "endDerivative": vector(4.06, 0.1) * mm});
            skSolve(sketch);
        }
        {
            var Q0;
            Q0 = qSketchRegion(id + "F8", true);
            var Q1;
            Q1=sQuery(id+"F8.wireOp",EDGE,"E81");
            var Q2;
            Q2=sQuery(id+"F8.wireOp",EDGE,"E70");
            var Q3;
            Q3=sQuery(id+"F8.wireOp",EDGE,"E71");
            var Q4;
            Q4=sQuery(id+"F8.wireOp",EDGE,"8d18383e-f7f6-428a-8497-72edc076fc2f");
            var Q5;
            Q5=sQuery(id+"F8.wireOp",EDGE,"E73");
            var Q6;
            Q6=sQuery(id+"F8.wireOp",EDGE,"E74");
            var Q7;
            Q7=sQuery(id+"F8.wireOp",EDGE,"E72");
            var Q8;
            Q8=sQuery(id+"F8.wireOp",EDGE,"E75");
            var Q9;
            Q9=sQuery(id+"F8.wireOp",EDGE,"E76");
            var Q10;
            Q10=sQuery(id+"F8.wireOp",EDGE,"E77");
            var Q11;
            Q11=sQuery(id+"F8.wireOp",EDGE,"E82");
            var Q12;
            Q12=sQuery(id+"F8.wireOp",EDGE,"E83");
            var Q13;
            Q13=sQuery(id+"F8.wireOp",EDGE,"E78");
            var Q14;
            Q14=sQuery(id+"F8.wireOp",EDGE,"E79");
            var Q15;
            Q15=sQuery(id+"F8.wireOp",EDGE,"E80");
            var Q16;
            Q16=sQuery(id+"F8.wireOp",EDGE,"E84");
            var Q17;
            Q17=sQuery(id+"F8.wireOp",EDGE,"E85");
            var Q18;
            Q18=sQuery(id+"F8.wireOp",EDGE,"E86");
            var Q19;
            Q19=sQuery(id+"F8.wireOp",EDGE,"E87");
            var Q20;
            Q20=sQuery(id+"F8.wireOp",EDGE,"f8b8ad0c-d252-4865-9b0d-6e5f7e19a82a");
            extrude(context, id + "F9", {"entities" : qUnion([Q0]), "bodyType" : ToolBodyType.SURFACE, "surfaceEntities" : qUnion([Q1, Q2, Q3, Q4, Q5, Q6, Q7, Q8, Q9, Q10, Q11, Q12, Q13, Q14, Q15, Q16, Q17, Q18, Q19, Q20]), "depth" : 0.25 * mm});
        }
    });
